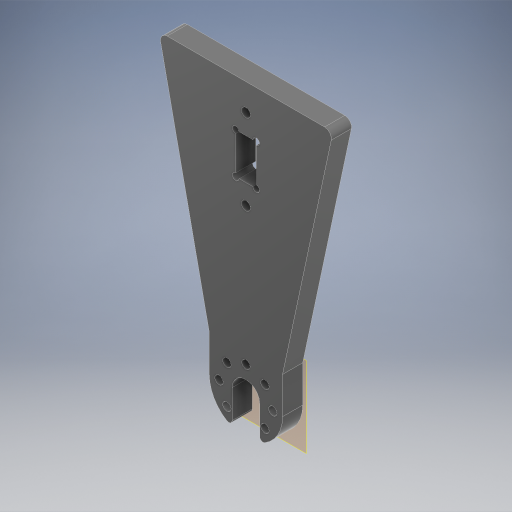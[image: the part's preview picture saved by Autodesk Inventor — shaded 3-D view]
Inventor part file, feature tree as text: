
AUTODESK INVENTOR PART (.ipt)
format: ipt  version: 2024 (Build 280153000, 153)  size: 334,336 bytes
history: native  units: in
note: dims shown in document units (in); Inventor stores cm internally (conversion verified against a paired STEP export)
features: other x3, extrude x2, fillet x2, sketch x2, reference x1
ambient origin geometry x8: Origin, YZ Plane, XZ Plane, XY Plane, X Axis, Y Axis, Z Axis, Center Point
bodies: Body1 (feature_tree)
feature tree (10):
  other  "작업 평면1"
  extrude  "돌출6"  Depth=0.1063in
  fillet  "모깎기2"  Radius=0.1063in
  fillet  "모깎기3"  Radius=0.2402in
  extrude  "돌출7"  Depth=0.4764in
  sketch  "스케치1"
  reference  "참조1"
  sketch  "스케치2"
  other  "조립품5"
  other  "28Horn:1"
